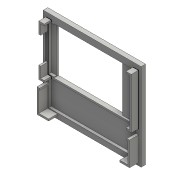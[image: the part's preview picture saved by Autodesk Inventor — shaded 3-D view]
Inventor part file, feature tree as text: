
AUTODESK INVENTOR PART (.ipt)
format: ipt  version: 2016 (Build 200138000, 138)  size: 221,184 bytes
history: native  units: mm
features: extrude x18, sketch x13
ambient origin geometry x8: Origin, YZ Plane, XZ Plane, XY Plane, X Axis, Y Axis, Z Axis, Center Point
bodies: Volumenkörper1 (feature_tree)
feature tree (31):
  extrude  "Extrusion1"  Depth=98.0mm
  sketch  "Skizze2"  dims[d2=5.0mm d3=0.0mm d4=8.0mm d5=0.0mm]
  extrude  "Extrusion2"  Depth=8.0mm TaperAngle=0.0deg
  extrude  "Extrusion3"  Depth=8.0mm TaperAngle=0.0deg
  extrude  "Extrusion4"  Depth=8.0mm TaperAngle=0.0deg
  extrude  "Extrusion5"  Depth=8.0mm TaperAngle=0.0deg
  extrude  "Extrusion6"  Depth=10.0mm TaperAngle=0.0deg
  extrude  "Extrusion7"  Depth=10.0mm TaperAngle=0.0deg
  extrude  "Extrusion8"  Depth=2.0mm TaperAngle=0.0deg
  extrude  "Extrusion9"  Depth=10.0mm TaperAngle=0.0deg
  extrude  "Extrusion10"  Depth=3.0mm TaperAngle=0.0deg
  extrude  "Extrusion11"  [1 undecoded]
  extrude  "Extrusion12"  [1 undecoded]
  extrude  "Extrusion13"  [1 undecoded]
  extrude  "Extrusion20"  [1 undecoded]
  extrude  "Extrusion21"  [1 undecoded]
  extrude  "Extrusion22"  [1 undecoded]
  extrude  "Extrusion23"  [1 undecoded]
  extrude  "Extrusion24"  [1 undecoded]
  sketch  "Skizze1"  dims[d0=110.0mm d1=98.0mm]
  sketch  "Skizze3"  dims[d6=8.0mm d7=0.0mm d8=8.0mm d9=0.0mm]
  sketch  "Skizze4"  dims[d10=8.0mm d11=0.0mm d12=8.0mm d13=0.0mm]
  sketch  "Skizze5"  dims[d14=8.0mm d15=0.0mm d16=8.0mm d17=0.0mm]
  sketch  "Skizze6"  dims[d18=8.0mm d19=0.0mm d20=10.0mm d21=0.0mm]
  sketch  "Skizze7"  dims[d22=10.0mm d23=0.0mm d24=10.0mm d25=0.0mm]
  sketch  "Skizze8"  dims[d26=10.0mm d27=0.0mm d49=2.0mm d50=0.0mm]
  sketch  "Skizze14"  dims[d51=3.0mm d52=0.0mm d53=10.0mm d54=0.0mm]
  sketch  "Skizze15"  dims[d55=3.0mm d56=0.0mm d57=3.0mm d58=0.0mm]
  sketch  "Skizze16"
  sketch  "Skizze17"
  sketch  "Skizze18"
note: 8 required parameter values undecoded (feature->parameter linkage not recoverable at this tier; creation-order binding heuristic only, values carry confidence <= 0.55)
